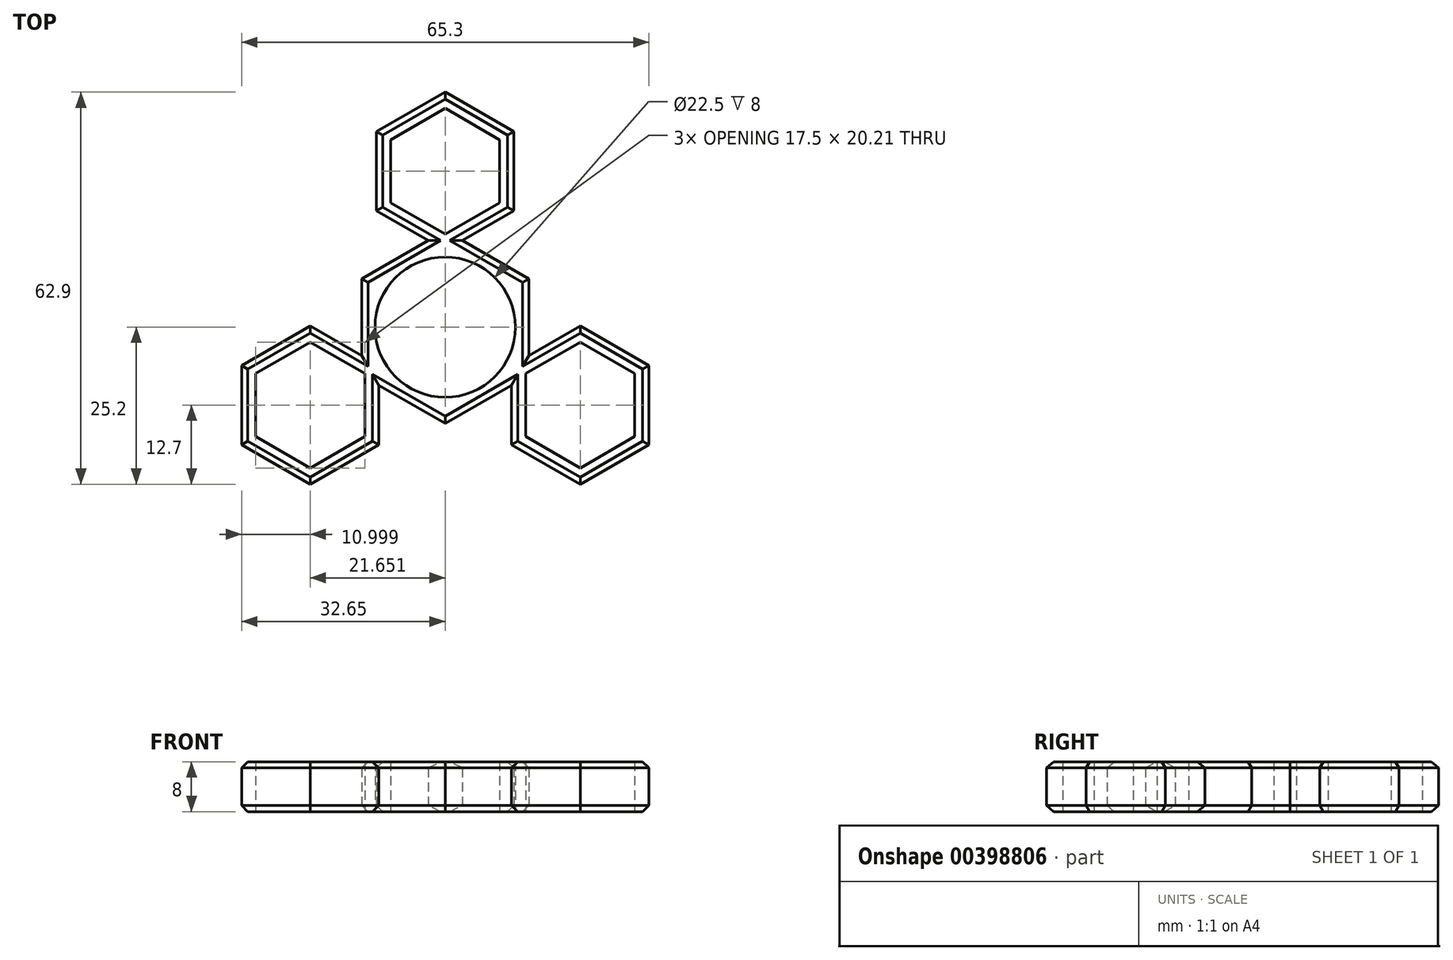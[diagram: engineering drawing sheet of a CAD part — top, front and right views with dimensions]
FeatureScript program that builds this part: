
annotation { "Feature Type Name" : "Feature", "Feature Type Description" : "" }
export const myFeature = defineFeature(function(context is Context, id is Id, definition is map)
    precondition{}
    {
        {
            var Q0;
            Q0=qCreatedBy(makeId("Top.planeOp"),FACE);
            var sketch = newSketch(context, id + "F0", { "sketchPlane" : qUnion([Q0])});
            skCircle(sketch, "E0", {"center": v(0, 0) * mm, "radius": 11.25 * mm});
            skPoint(sketch, "E1.0.midPoint", {"position": v(0, 13) * mm});
            skLineSegment(sketch, "E2", {"start": v(0, 0) * mm, "end": v(0, 25) * mm});
            skCircle(sketch, "E3.cCircle", {"center": v(0, 25) * mm, "radius": 8.75 * mm, "construction": true});
            skLineSegment(sketch, "E3.0", {"start": v(0, 14.9) * mm, "end": v(-8.75, 19.95) * mm});
            skLineSegment(sketch, "E3.1", {"start": v(-8.75, 19.95) * mm, "end": v(-8.75, 30.05) * mm});
            skLineSegment(sketch, "E3.2", {"start": v(-8.75, 30.05) * mm, "end": v(0, 35.1) * mm});
            skLineSegment(sketch, "E3.3", {"start": v(0, 35.1) * mm, "end": v(8.75, 30.05) * mm});
            skLineSegment(sketch, "E3.4", {"start": v(8.75, 30.05) * mm, "end": v(8.75, 19.95) * mm});
            skLineSegment(sketch, "E3.5", {"start": v(8.75, 19.95) * mm, "end": v(0, 14.9) * mm});
            skPoint(sketch, "E3.0.midPoint", {"position": v(-4.37, 17.42) * mm});
            skCircle(sketch, "E4.cCircle", {"center": v(0, 25) * mm, "radius": 11 * mm, "construction": true});
            skLineSegment(sketch, "E4.0", {"start": v(0, 12.3) * mm, "end": v(-11, 18.65) * mm});
            skLineSegment(sketch, "E4.1", {"start": v(-11, 18.65) * mm, "end": v(-11, 31.35) * mm});
            skLineSegment(sketch, "E4.2", {"start": v(-11, 31.35) * mm, "end": v(0, 37.7) * mm});
            skLineSegment(sketch, "E4.3", {"start": v(0, 37.7) * mm, "end": v(11, 31.35) * mm});
            skLineSegment(sketch, "E4.4", {"start": v(11, 31.35) * mm, "end": v(11, 18.65) * mm});
            skLineSegment(sketch, "E4.5", {"start": v(11, 18.65) * mm, "end": v(0, 12.3) * mm});
            skPoint(sketch, "E4.0.midPoint", {"position": v(-5.5, 15.47) * mm});
            skLineSegment(sketch, "E5.1.0", {"start": v(-30.4, -7.45) * mm, "end": v(-21.65, -2.4) * mm});
            skLineSegment(sketch, "E5.1.1", {"start": v(-10.65, -18.85) * mm, "end": v(-21.65, -25.2) * mm});
            skLineSegment(sketch, "E5.1.2", {"start": v(-12.9, -7.45) * mm, "end": v(-12.9, -17.55) * mm});
            skLineSegment(sketch, "E5.1.3", {"start": v(-21.65, -25.2) * mm, "end": v(-32.65, -18.85) * mm});
            skLineSegment(sketch, "E5.1.4", {"start": v(-32.65, -6.15) * mm, "end": v(-21.65, 0.2) * mm});
            skCircle(sketch, "E5.1.5", {"center": v(-21.65, -12.5) * mm, "radius": 11 * mm, "construction": true});
            skLineSegment(sketch, "E5.1.6", {"start": v(-32.65, -18.85) * mm, "end": v(-32.65, -6.15) * mm});
            skPoint(sketch, "E5.1.7", {"position": v(-11.25, -6.5) * mm});
            skPoint(sketch, "E5.1.8", {"position": v(-12.9, -12.5) * mm});
            skPoint(sketch, "E5.1.9", {"position": v(-10.65, -12.5) * mm});
            skLineSegment(sketch, "E5.1.10", {"start": v(-30.4, -17.55) * mm, "end": v(-30.4, -7.45) * mm});
            skLineSegment(sketch, "E5.1.11", {"start": v(-21.65, -2.4) * mm, "end": v(-12.9, -7.45) * mm});
            skLineSegment(sketch, "E5.1.12", {"start": v(-10.65, -6.15) * mm, "end": v(-10.65, -18.85) * mm});
            skLineSegment(sketch, "E5.1.13", {"start": v(-21.65, -22.6) * mm, "end": v(-30.4, -17.55) * mm});
            skCircle(sketch, "E5.1.14", {"center": v(-21.65, -12.5) * mm, "radius": 8.75 * mm, "construction": true});
            skLineSegment(sketch, "E5.1.15", {"start": v(-21.65, 0.2) * mm, "end": v(-10.65, -6.15) * mm});
            skLineSegment(sketch, "E5.1.16", {"start": v(-12.9, -17.55) * mm, "end": v(-21.65, -22.6) * mm});
            skLineSegment(sketch, "E5.2.0", {"start": v(21.65, -22.6) * mm, "end": v(12.9, -17.55) * mm});
            skLineSegment(sketch, "E5.2.1", {"start": v(21.65, 0.2) * mm, "end": v(32.65, -6.15) * mm});
            skLineSegment(sketch, "E5.2.2", {"start": v(12.9, -7.45) * mm, "end": v(21.65, -2.4) * mm});
            skLineSegment(sketch, "E5.2.3", {"start": v(32.65, -6.15) * mm, "end": v(32.65, -18.85) * mm});
            skLineSegment(sketch, "E5.2.4", {"start": v(21.65, -25.2) * mm, "end": v(10.65, -18.85) * mm});
            skCircle(sketch, "E5.2.5", {"center": v(21.65, -12.5) * mm, "radius": 11 * mm, "construction": true});
            skLineSegment(sketch, "E5.2.6", {"start": v(32.65, -18.85) * mm, "end": v(21.65, -25.2) * mm});
            skPoint(sketch, "E5.2.7", {"position": v(11.25, -6.5) * mm});
            skPoint(sketch, "E5.2.8", {"position": v(17.28, -4.92) * mm});
            skPoint(sketch, "E5.2.9", {"position": v(16.15, -2.97) * mm});
            skLineSegment(sketch, "E5.2.10", {"start": v(30.4, -17.55) * mm, "end": v(21.65, -22.6) * mm});
            skLineSegment(sketch, "E5.2.11", {"start": v(12.9, -17.55) * mm, "end": v(12.9, -7.45) * mm});
            skLineSegment(sketch, "E5.2.12", {"start": v(10.65, -6.15) * mm, "end": v(21.65, 0.2) * mm});
            skLineSegment(sketch, "E5.2.13", {"start": v(30.4, -7.45) * mm, "end": v(30.4, -17.55) * mm});
            skCircle(sketch, "E5.2.14", {"center": v(21.65, -12.5) * mm, "radius": 8.75 * mm, "construction": true});
            skLineSegment(sketch, "E5.2.15", {"start": v(10.65, -18.85) * mm, "end": v(10.65, -6.15) * mm});
            skLineSegment(sketch, "E5.2.16", {"start": v(21.65, -2.4) * mm, "end": v(30.4, -7.45) * mm});
            skCircle(sketch, "E6.cCircle", {"center": v(0, 0) * mm, "radius": 13.39 * mm, "construction": true});
            skLineSegment(sketch, "E6.0", {"start": v(-13.39, 7.73) * mm, "end": v(0, 15.46) * mm});
            skLineSegment(sketch, "E6.1", {"start": v(0, 15.46) * mm, "end": v(13.39, 7.73) * mm});
            skLineSegment(sketch, "E6.2", {"start": v(13.39, 7.73) * mm, "end": v(13.39, -7.73) * mm});
            skLineSegment(sketch, "E6.3", {"start": v(13.39, -7.73) * mm, "end": v(0, -15.46) * mm});
            skLineSegment(sketch, "E6.4", {"start": v(0, -15.46) * mm, "end": v(-13.39, -7.73) * mm});
            skLineSegment(sketch, "E6.5", {"start": v(-13.39, -7.73) * mm, "end": v(-13.39, 7.73) * mm});
            skPoint(sketch, "E6.0.midPoint", {"position": v(-6.7, 11.6) * mm});
            skSolve(sketch);
        }
        {
            var Q0;
            Q0 = qSketchRegion(id + "F0", true);
            var Q1;
            {var subQ0=sQuery(id+"F0.wireOp",EDGE,"E5.1.15");var subQ1=sQuery(id+"F0.wireOp",EDGE,"lxdlBeQJ-3IsZ-dX6P-ghJB-0KyvdBaH4FO6");var subQ2=makeQuery(id+"F0.imprint","INTERSECT",VERTEX,{"derivedFrom":[subQ1,subQ0]});Q1=makeQuery(id+"F0.imprint","IMPRINT",FACE,{"disambiguationData":[TD([[makeQuery(id+"F0.imprint","IMPRINT",EDGE,{"disambiguationData":[TD([[subQ2,-1.0]])],"derivedFrom":subQ1}),1.0]])]});}
            var Q2;
            {var subQ0=sQuery(id+"F0.wireOp",EDGE,"E5.2.15");var subQ1=sQuery(id+"F0.wireOp",EDGE,"lxdlBeQJ-3IsZ-dX6P-ghJB-0KyvdBaH4FO6");var subQ2=makeQuery(id+"F0.imprint","INTERSECT",VERTEX,{"derivedFrom":[subQ1,subQ0]});Q2=makeQuery(id+"F0.imprint","IMPRINT",FACE,{"disambiguationData":[TD([[makeQuery(id+"F0.imprint","IMPRINT",EDGE,{"disambiguationData":[TD([[subQ2,-1.0]])],"derivedFrom":subQ1}),1.0]])]});}
            var Q3;
            {var subQ0=sQuery(id+"F0.wireOp",EDGE,"E2");var subQ1=sQuery(id+"F0.wireOp",EDGE,"lxdlBeQJ-3IsZ-dX6P-ghJB-0KyvdBaH4FO6");var subQ2=makeQuery(id+"F0.imprint","INTERSECT",VERTEX,{"derivedFrom":[subQ1,subQ0]});Q3=makeQuery(id+"F0.imprint","IMPRINT",FACE,{"disambiguationData":[TD([[makeQuery(id+"F0.imprint","IMPRINT",EDGE,{"disambiguationData":[TD([[subQ2,-1.0]])],"derivedFrom":subQ1}),1.0]])]});}
            var Q4;
            Q4=makeQuery(id+"F0.imprint","IMPRINT",FACE,{"disambiguationData":[TD([[makeQuery(id+"F0.imprint","IMPRINT",EDGE,{"derivedFrom":sQuery(id+"F0.wireOp",EDGE,"E0")}),-1.0]])]});
            var Q5;
            {var subQ0=sQuery(id+"F0.wireOp",EDGE,"E2");var subQ1=sQuery(id+"F0.wireOp",EDGE,"lxdlBeQJ-3IsZ-dX6P-ghJB-0KyvdBaH4FO6");var subQ2=makeQuery(id+"F0.imprint","INTERSECT",VERTEX,{"derivedFrom":[subQ1,subQ0]});Q5=makeQuery(id+"F0.imprint","IMPRINT",FACE,{"disambiguationData":[TD([[makeQuery(id+"F0.imprint","IMPRINT",EDGE,{"disambiguationData":[TD([[subQ2,1.0]])],"derivedFrom":subQ1}),1.0]])]});}
            var Q6;
            {var subQ0=sQuery(id+"F0.wireOp",EDGE,"E5.1.15");var subQ1=sQuery(id+"F0.wireOp",EDGE,"E5.1.12");var subQ2=makeQuery(id+"F0.imprint","INTERSECT",VERTEX,{"derivedFrom":[subQ1,subQ0]});Q6=makeQuery(id+"F0.imprint","IMPRINT",FACE,{"disambiguationData":[TD([[makeQuery(id+"F0.imprint","IMPRINT",EDGE,{"disambiguationData":[TD([[subQ2,-1.0]])],"derivedFrom":subQ1}),-1.0]])]});}
            var Q7;
            {var subQ0=sQuery(id+"F0.wireOp",EDGE,"E4.0");var subQ3=sQuery(id+"F0.wireOp",EDGE,"E6.0");var subQ5=makeQuery(id+"F0.imprint","INTERSECT",VERTEX,{"derivedFrom":[subQ0,subQ3]});Q7=makeQuery(id+"F0.imprint","IMPRINT",FACE,{"disambiguationData":[TD([[makeQuery(id+"F0.imprint","IMPRINT",EDGE,{"disambiguationData":[TD([[subQ5,1.0]])],"derivedFrom":subQ0}),-1.0]])]});}
            var Q8;
            {var subQ0=sQuery(id+"F0.wireOp",EDGE,"E5.2.15");var subQ1=sQuery(id+"F0.wireOp",EDGE,"E5.2.12");var subQ2=makeQuery(id+"F0.imprint","INTERSECT",VERTEX,{"derivedFrom":[subQ1,subQ0]});Q8=makeQuery(id+"F0.imprint","IMPRINT",FACE,{"disambiguationData":[TD([[makeQuery(id+"F0.imprint","IMPRINT",EDGE,{"disambiguationData":[TD([[subQ2,-1.0]])],"derivedFrom":subQ1}),-1.0]])]});}
            var Q9;
            {var subQ0=sQuery(id+"F0.wireOp",EDGE,"E4.5");var subQ3=sQuery(id+"F0.wireOp",EDGE,"E6.1");var subQ5=makeQuery(id+"F0.imprint","INTERSECT",VERTEX,{"derivedFrom":[subQ0,subQ3]});Q9=makeQuery(id+"F0.imprint","IMPRINT",FACE,{"disambiguationData":[TD([[makeQuery(id+"F0.imprint","IMPRINT",EDGE,{"disambiguationData":[TD([[subQ5,-1.0]])],"derivedFrom":subQ0}),-1.0]])]});}
            extrude(context, id + "F1", {"entities" : qUnion([Q0, Q1, Q2, Q3, Q4, Q5, Q6, Q7, Q8, Q9]), "depth" : 8 * mm});
        }
        {
            var Q0;
            Q0=makeQuery(id+"F1.opExtrude","CAP_EDGE",EDGE,{"disambiguationData":[OSD([sQuery(id+"F0.wireOp",EDGE,"E6.0")])],"isStart":false});
            var Q1;
            Q1=makeQuery(id+"F1.opExtrude","CAP_EDGE",EDGE,{"disambiguationData":[OSD([sQuery(id+"F0.wireOp",EDGE,"E6.5")])],"isStart":false});
            var Q2;
            Q2=makeQuery(id+"F1.opExtrude","CAP_EDGE",EDGE,{"disambiguationData":[OSD([sQuery(id+"F0.wireOp",EDGE,"E5.1.15")])],"isStart":false});
            var Q3;
            Q3=makeQuery(id+"F1.opExtrude","CAP_EDGE",EDGE,{"disambiguationData":[OSD([sQuery(id+"F0.wireOp",EDGE,"E5.1.4")])],"isStart":false});
            var Q4;
            Q4=makeQuery(id+"F1.opExtrude","CAP_EDGE",EDGE,{"disambiguationData":[OSD([sQuery(id+"F0.wireOp",EDGE,"E5.1.6")])],"isStart":false});
            var Q5;
            Q5=makeQuery(id+"F1.opExtrude","CAP_EDGE",EDGE,{"disambiguationData":[OSD([sQuery(id+"F0.wireOp",EDGE,"E5.1.3")])],"isStart":false});
            var Q6;
            Q6=makeQuery(id+"F1.opExtrude","CAP_EDGE",EDGE,{"disambiguationData":[OSD([sQuery(id+"F0.wireOp",EDGE,"E5.1.1")])],"isStart":false});
            var Q7;
            Q7=makeQuery(id+"F1.opExtrude","CAP_EDGE",EDGE,{"disambiguationData":[OSD([sQuery(id+"F0.wireOp",EDGE,"E6.4")])],"isStart":false});
            var Q8;
            Q8=makeQuery(id+"F1.opExtrude","CAP_EDGE",EDGE,{"disambiguationData":[OSD([sQuery(id+"F0.wireOp",EDGE,"E5.1.12")])],"isStart":false});
            var Q9;
            Q9=makeQuery(id+"F1.opExtrude","CAP_EDGE",EDGE,{"disambiguationData":[OSD([sQuery(id+"F0.wireOp",EDGE,"E6.3")])],"isStart":false});
            var Q10;
            Q10=makeQuery(id+"F1.opExtrude","CAP_EDGE",EDGE,{"disambiguationData":[OSD([sQuery(id+"F0.wireOp",EDGE,"E5.2.15")])],"isStart":false});
            var Q11;
            Q11=makeQuery(id+"F1.opExtrude","CAP_EDGE",EDGE,{"disambiguationData":[OSD([sQuery(id+"F0.wireOp",EDGE,"E5.2.4")])],"isStart":false});
            var Q12;
            Q12=makeQuery(id+"F1.opExtrude","CAP_EDGE",EDGE,{"disambiguationData":[OSD([sQuery(id+"F0.wireOp",EDGE,"E5.2.6")])],"isStart":false});
            var Q13;
            Q13=makeQuery(id+"F1.opExtrude","CAP_EDGE",EDGE,{"disambiguationData":[OSD([sQuery(id+"F0.wireOp",EDGE,"E5.2.3")])],"isStart":false});
            var Q14;
            Q14=makeQuery(id+"F1.opExtrude","CAP_EDGE",EDGE,{"disambiguationData":[OSD([sQuery(id+"F0.wireOp",EDGE,"E5.2.1")])],"isStart":false});
            var Q15;
            Q15=makeQuery(id+"F1.opExtrude","CAP_EDGE",EDGE,{"disambiguationData":[OSD([sQuery(id+"F0.wireOp",EDGE,"E5.2.12")])],"isStart":false});
            var Q16;
            Q16=makeQuery(id+"F1.opExtrude","CAP_EDGE",EDGE,{"disambiguationData":[OSD([sQuery(id+"F0.wireOp",EDGE,"E6.2")])],"isStart":false});
            var Q17;
            Q17=makeQuery(id+"F1.opExtrude","CAP_EDGE",EDGE,{"disambiguationData":[OSD([sQuery(id+"F0.wireOp",EDGE,"E6.1")])],"isStart":false});
            var Q18;
            Q18=makeQuery(id+"F1.opExtrude","CAP_EDGE",EDGE,{"disambiguationData":[OSD([sQuery(id+"F0.wireOp",EDGE,"E4.5")])],"isStart":false});
            var Q19;
            Q19=makeQuery(id+"F1.opExtrude","CAP_EDGE",EDGE,{"disambiguationData":[OSD([sQuery(id+"F0.wireOp",EDGE,"E4.4")])],"isStart":false});
            var Q20;
            Q20=makeQuery(id+"F1.opExtrude","CAP_EDGE",EDGE,{"disambiguationData":[OSD([sQuery(id+"F0.wireOp",EDGE,"E4.3")])],"isStart":false});
            var Q21;
            Q21=makeQuery(id+"F1.opExtrude","CAP_EDGE",EDGE,{"disambiguationData":[OSD([sQuery(id+"F0.wireOp",EDGE,"E4.2")])],"isStart":false});
            var Q22;
            Q22=makeQuery(id+"F1.opExtrude","CAP_EDGE",EDGE,{"disambiguationData":[OSD([sQuery(id+"F0.wireOp",EDGE,"E4.1")])],"isStart":false});
            var Q23;
            Q23=makeQuery(id+"F1.opExtrude","CAP_EDGE",EDGE,{"disambiguationData":[OSD([sQuery(id+"F0.wireOp",EDGE,"E4.0")])],"isStart":false});
            var Q24;
            Q24=makeQuery(id+"F1.opExtrude","CAP_EDGE",EDGE,{"disambiguationData":[OSD([sQuery(id+"F0.wireOp",EDGE,"E4.1")])],"isStart":true});
            var Q25;
            Q25=makeQuery(id+"F1.opExtrude","CAP_EDGE",EDGE,{"disambiguationData":[OSD([sQuery(id+"F0.wireOp",EDGE,"E4.2")])],"isStart":true});
            var Q26;
            Q26=makeQuery(id+"F1.opExtrude","CAP_EDGE",EDGE,{"disambiguationData":[OSD([sQuery(id+"F0.wireOp",EDGE,"E4.3")])],"isStart":true});
            var Q27;
            Q27=makeQuery(id+"F1.opExtrude","CAP_EDGE",EDGE,{"disambiguationData":[OSD([sQuery(id+"F0.wireOp",EDGE,"E4.4")])],"isStart":true});
            var Q28;
            Q28=makeQuery(id+"F1.opExtrude","CAP_EDGE",EDGE,{"disambiguationData":[OSD([sQuery(id+"F0.wireOp",EDGE,"E4.5")])],"isStart":true});
            var Q29;
            Q29=makeQuery(id+"F1.opExtrude","CAP_EDGE",EDGE,{"disambiguationData":[OSD([sQuery(id+"F0.wireOp",EDGE,"E4.0")])],"isStart":true});
            var Q30;
            Q30=makeQuery(id+"F1.opExtrude","CAP_EDGE",EDGE,{"disambiguationData":[OSD([sQuery(id+"F0.wireOp",EDGE,"E6.0")])],"isStart":true});
            var Q31;
            Q31=makeQuery(id+"F1.opExtrude","CAP_EDGE",EDGE,{"disambiguationData":[OSD([sQuery(id+"F0.wireOp",EDGE,"E6.1")])],"isStart":true});
            var Q32;
            Q32=makeQuery(id+"F1.opExtrude","CAP_EDGE",EDGE,{"disambiguationData":[OSD([sQuery(id+"F0.wireOp",EDGE,"E6.2")])],"isStart":true});
            var Q33;
            Q33=makeQuery(id+"F1.opExtrude","CAP_EDGE",EDGE,{"disambiguationData":[OSD([sQuery(id+"F0.wireOp",EDGE,"E6.5")])],"isStart":true});
            var Q34;
            Q34=makeQuery(id+"F1.opExtrude","CAP_EDGE",EDGE,{"disambiguationData":[OSD([sQuery(id+"F0.wireOp",EDGE,"E5.2.12")])],"isStart":true});
            var Q35;
            Q35=makeQuery(id+"F1.opExtrude","CAP_EDGE",EDGE,{"disambiguationData":[OSD([sQuery(id+"F0.wireOp",EDGE,"E5.2.1")])],"isStart":true});
            var Q36;
            Q36=makeQuery(id+"F1.opExtrude","CAP_EDGE",EDGE,{"disambiguationData":[OSD([sQuery(id+"F0.wireOp",EDGE,"E5.2.3")])],"isStart":true});
            var Q37;
            Q37=makeQuery(id+"F1.opExtrude","CAP_EDGE",EDGE,{"disambiguationData":[OSD([sQuery(id+"F0.wireOp",EDGE,"E5.2.6")])],"isStart":true});
            var Q38;
            Q38=makeQuery(id+"F1.opExtrude","CAP_EDGE",EDGE,{"disambiguationData":[OSD([sQuery(id+"F0.wireOp",EDGE,"E5.2.4")])],"isStart":true});
            var Q39;
            Q39=makeQuery(id+"F1.opExtrude","CAP_EDGE",EDGE,{"disambiguationData":[OSD([sQuery(id+"F0.wireOp",EDGE,"E5.2.15")])],"isStart":true});
            var Q40;
            Q40=makeQuery(id+"F1.opExtrude","CAP_EDGE",EDGE,{"disambiguationData":[OSD([sQuery(id+"F0.wireOp",EDGE,"E6.3")])],"isStart":true});
            var Q41;
            Q41=makeQuery(id+"F1.opExtrude","CAP_EDGE",EDGE,{"disambiguationData":[OSD([sQuery(id+"F0.wireOp",EDGE,"E6.4")])],"isStart":true});
            var Q42;
            Q42=makeQuery(id+"F1.opExtrude","CAP_EDGE",EDGE,{"disambiguationData":[OSD([sQuery(id+"F0.wireOp",EDGE,"E5.1.12")])],"isStart":true});
            var Q43;
            Q43=makeQuery(id+"F1.opExtrude","CAP_EDGE",EDGE,{"disambiguationData":[OSD([sQuery(id+"F0.wireOp",EDGE,"E5.1.1")])],"isStart":true});
            var Q44;
            Q44=makeQuery(id+"F1.opExtrude","CAP_EDGE",EDGE,{"disambiguationData":[OSD([sQuery(id+"F0.wireOp",EDGE,"E5.1.3")])],"isStart":true});
            var Q45;
            Q45=makeQuery(id+"F1.opExtrude","CAP_EDGE",EDGE,{"disambiguationData":[OSD([sQuery(id+"F0.wireOp",EDGE,"E5.1.6")])],"isStart":true});
            var Q46;
            Q46=makeQuery(id+"F1.opExtrude","CAP_EDGE",EDGE,{"disambiguationData":[OSD([sQuery(id+"F0.wireOp",EDGE,"E5.1.4")])],"isStart":true});
            var Q47;
            Q47=makeQuery(id+"F1.opExtrude","CAP_EDGE",EDGE,{"disambiguationData":[OSD([sQuery(id+"F0.wireOp",EDGE,"E5.1.15")])],"isStart":true});
            var Q48;
            Q48=makeQuery(id+"F1.opExtrude","CAP_EDGE",EDGE,{"disambiguationData":[OSD([sQuery(id+"F0.wireOp",EDGE,"gOjXQbGW-eZm3-FbEg-B6ck-nj6HoVHWhSur")])],"isStart":false});
            var Q49;
            Q49=makeQuery(id+"F1.opExtrude","CAP_EDGE",EDGE,{"disambiguationData":[OSD([sQuery(id+"F0.wireOp",EDGE,"biIzwVks-4y24-8gTH-hxSi-bubsSAKFYUO2")])],"isStart":false});
            var Q50;
            Q50=makeQuery(id+"F1.opExtrude","CAP_EDGE",EDGE,{"disambiguationData":[OSD([sQuery(id+"F0.wireOp",EDGE,"Qfa4eciT-AWF6-1J2W-a0Sy-KoLGvY3xYQLS")])],"isStart":false});
            var Q51;
            Q51=makeQuery(id+"F1.opExtrude","CAP_EDGE",EDGE,{"disambiguationData":[OSD([sQuery(id+"F0.wireOp",EDGE,"Qfa4eciT-AWF6-1J2W-a0Sy-KoLGvY3xYQLS")])],"isStart":true});
            var Q52;
            Q52=makeQuery(id+"F1.opExtrude","CAP_EDGE",EDGE,{"disambiguationData":[OSD([sQuery(id+"F0.wireOp",EDGE,"biIzwVks-4y24-8gTH-hxSi-bubsSAKFYUO2")])],"isStart":true});
            var Q53;
            Q53=makeQuery(id+"F1.opExtrude","CAP_EDGE",EDGE,{"disambiguationData":[OSD([sQuery(id+"F0.wireOp",EDGE,"gOjXQbGW-eZm3-FbEg-B6ck-nj6HoVHWhSur")])],"isStart":true});
            chamfer(context, id + "F2", {"entities" : qUnion([Q0, Q1, Q2, Q3, Q4, Q5, Q6, Q7, Q8, Q9, Q10, Q11, Q12, Q13, Q14, Q15, Q16, Q17, Q18, Q19, Q20, Q21, Q22, Q23, Q24, Q25, Q26, Q27, Q28, Q29, Q30, Q31, Q32, Q33, Q34, Q35, Q36, Q37, Q38, Q39, Q40, Q41, Q42, Q43, Q44, Q45, Q46, Q47, Q48, Q49, Q50, Q51, Q52, Q53]), "width" : 1 * mm, "tangentPropagation" : true});
        }
    });
